# Revit family: TD92_LAU032_VER040_RVT20_R00
name_source: partatom
category: Mobiliário
units: mm (PartAtom-declared; Revit-internal decimal feet)

## family parameters
Com base no plano de trabalho = Não
Compartilhado = Não
Corte com vazios quando carregada = Não
Número OmniClass = 23.40.20.00
Ponto de cálculo do ambiente = Não
Sempre na vertical = Sim
Título OmniClass = General Furniture and Specialties

## types (1)
- TD92_LAU032_VER040_RVT20_R00
    Descrição = Você quer uma cadeira que vai dar à sua decoração um toque especial, charmoso e com muita personalidade? Pois saiba que além de tudo isso, com a Cadeira Tramontina Laura Rattan, da linha Summa, você tem um item muito resistente, produzido em polipropileno e fibra de vidro, o que garante suportar uma carga estática de até 182 kg. Tem textura lembrando rattan, o que dá característica marcante a ela. Não deixe pra depois, comece hoje a aliar elegância e praticidade à sua decoração.
    Elevação padrão = 0  [stored 0 ft]
    Fabricante = Tramontina Delta S/A
    Modelo = Cadeira Tramontina Laura Rattan em Polipropileno e Fibra de Vidro Vermelho
    Nota-chave = 92032040
    URL = https://www.tramontinastore.com

note: [stored X ft] marks values corroborated as IEEE doubles in the binary element streams (Revit-internal decimal feet)
